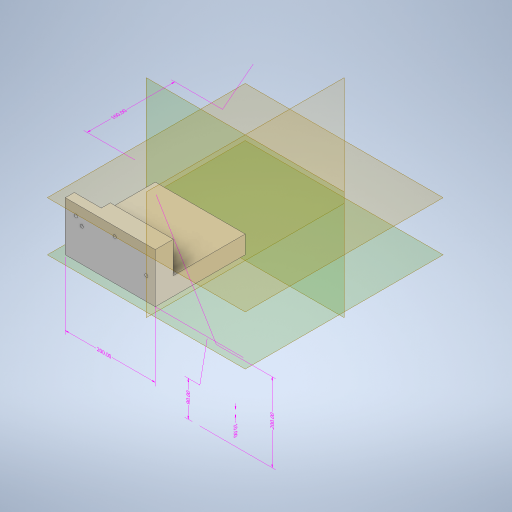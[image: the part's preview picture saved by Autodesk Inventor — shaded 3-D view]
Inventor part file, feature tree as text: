
AUTODESK INVENTOR PART (.ipt)
format: ipt  version: 2023 (Build 270158000, 158)  size: 451,072 bytes
history: native  units: mm
features: sketch x9, other x8, extrude x5, hole x4, plane x4, split x4
ambient origin geometry x8: Origin, YZ Plane, XZ Plane, XY Plane, X Axis, Y Axis, Z Axis, Center Point
bodies: Body1 (feature_tree)
feature tree (34):
  other  "Sólido1"
  other  "Anotaciones"
  extrude  "Extrusión1"  Depth=200.0mm
  hole  "Agujero1"  [1 undecoded]
  extrude  "Extrusión2"  Depth=15.0mm
  extrude  "Extrusión3"  Depth=80.0mm TaperAngle=0.0deg
  extrude  "Extrusión4"  Depth=200.0mm
  extrude  "Extrusión5"  Depth=20.0mm
  hole  "Agujero2"  [1 undecoded]
  plane  "Plano de trabajo1"
  split  "Dividir1"
  plane  "Plano de trabajo2"
  plane  "Plano de trabajo3"
  plane  "Plano de trabajo4"
  hole  "Agujero3"  [1 undecoded]
  hole  "Agujero4"  [1 undecoded]
  split  "Dividir2"
  split  "Dividir3"
  split  "Dividir4"
  sketch  "Boceto2"  dims[d7=15.0mm d8=200.0mm]
  sketch  "Boceto3"  dims[d9=10.0mm d10=0.0mm]
  sketch  "Boceto4"  dims[d11=3.5mm d12=1.75mm d13=1.75mm d14=1.75mm d15=1.75mm d16=10.0mm d17=10.0mm d19=40.0mm]
  sketch  "Boceto5"  dims[d20=3.5mm d21=6.0mm d22=4.0mm d23=2.0mm d24=90.0deg d25=8.0mm d26=20.594885mm d27=15.0mm]
  sketch  "Boceto6"  dims[d28=20.0mm d29=80.0mm d30=0.0mm]
  sketch  "Boceto7"  dims[d31=57.0mm d32=200.0mm]
  sketch  "Boceto8"  dims[d33=110.0mm d34=0.0mm d36=20.0mm]
  sketch  "Boceto9"  dims[d37=20.0mm d38=20.0mm]
  sketch  "Boceto10"  dims[d39=90.0mm d40=0.0mm d43=30.0mm d44=0.0mm d45=3.5mm d46=1.75mm d47=1.75mm d48=1.75mm d49=1.75mm d50=10.0mm d51=10.0mm d52=15.0mm d53=10.0mm d54=10.0mm d55=15.0mm d56=3.5mm d57=6.0mm d58=4.0mm d59=2.0mm d60=90.0deg d61=8.0mm d62=20.594885mm d63=10.0mm d65=10.0mm d75=200.0mm d76=10.0mm d77=20.0mm d81=40.0mm d88=90.0deg d89=10.0mm d90=30.0mm d91=5.0mm d92=5.0mm d93=5.0mm d94=5.0mm d95=30.0mm d96=5.0mm d97=5.0mm d98=3.5mm d99=5.0mm d100=5.0mm d101=5.0mm d102=5.0mm d103=5.0mm d104=20.0mm d105=3.5mm d106=6.0mm d107=4.0mm d108=2.0mm d109=90.0deg d110=8.0mm d111=20.594885mm d112=10.0mm d113=30.0mm d114=5.0mm d115=5.0mm d116=5.0mm d117=5.0mm d118=5.0mm d119=5.0mm d120=3.5mm d121=5.0mm d122=5.0mm d123=5.0mm d124=5.0mm d125=5.0mm d126=30.0mm d127=30.0mm d128=3.5mm d129=6.0mm d130=4.0mm d131=2.0mm d132=90.0deg d133=8.0mm d134=20.594885mm d66=5.760865mm d67=7.72461mm d68=200.0mm d69=3.008686mm d70=2.422102mm d71=10.0mm d72=3.500509mm d73=2.402572mm d74=90.0mm d78=3.13122mm d79=6.269346mm d80=200.0mm d82=8.450127mm d83=0.968417mm d84=20.0mm d85=4.759975mm d86=4.646891mm d87=160.0mm]
  other  "Cota lineal 1"
  other  "Cota lineal 2"
  other  "Cota lineal 3"
  other  "Cota lineal 4"
  other  "Cota lineal 5"
  other  "Cota lineal 6"
note: 4 required parameter values undecoded (feature->parameter linkage not recoverable at this tier; creation-order binding heuristic only, values carry confidence <= 0.55)
